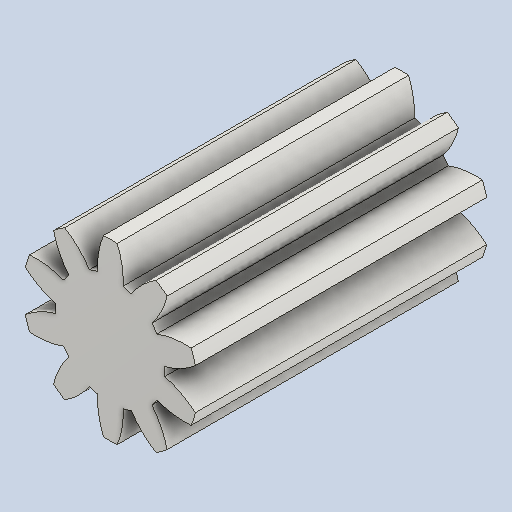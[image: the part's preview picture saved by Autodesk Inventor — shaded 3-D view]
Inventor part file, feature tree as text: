
AUTODESK INVENTOR PART (.ipt)
format: ipt  version: 2024 (Build 280153000, 153)  size: 235,008 bytes
history: native  units: mm (DEFAULTED — no unit token found)
features: plane x3, other x3, extrude x1, sketch x1
ambient origin geometry x8: Origin, YZ Plane, XZ Plane, XY Plane, X Axis, Y Axis, Z Axis, Center Point
bodies: Solid1 (feature_tree)
feature tree (8):
  extrude  "Extrusion1"  Depth=40.0mm TaperAngle=0.0deg
  plane  "Work Plane2"
  plane  "Work Plane8"
  plane  "Work Plane9"
  other  "Spur Gear"
  sketch  "Sketch1"  dims[d0=24.0mm d1=40.0mm d2=0.0mm d3=20.0mm d4=10.0mm d5=0.0mm d16=35.0mm d17=0.0mm d34=3.141593mm d39=0.0mm d41=0.0mm d43=35.0mm d46=35.0mm d47=0.0mm d48=0.0mm]
  other  "Srf1"
  other  "Pitch Diameter"
